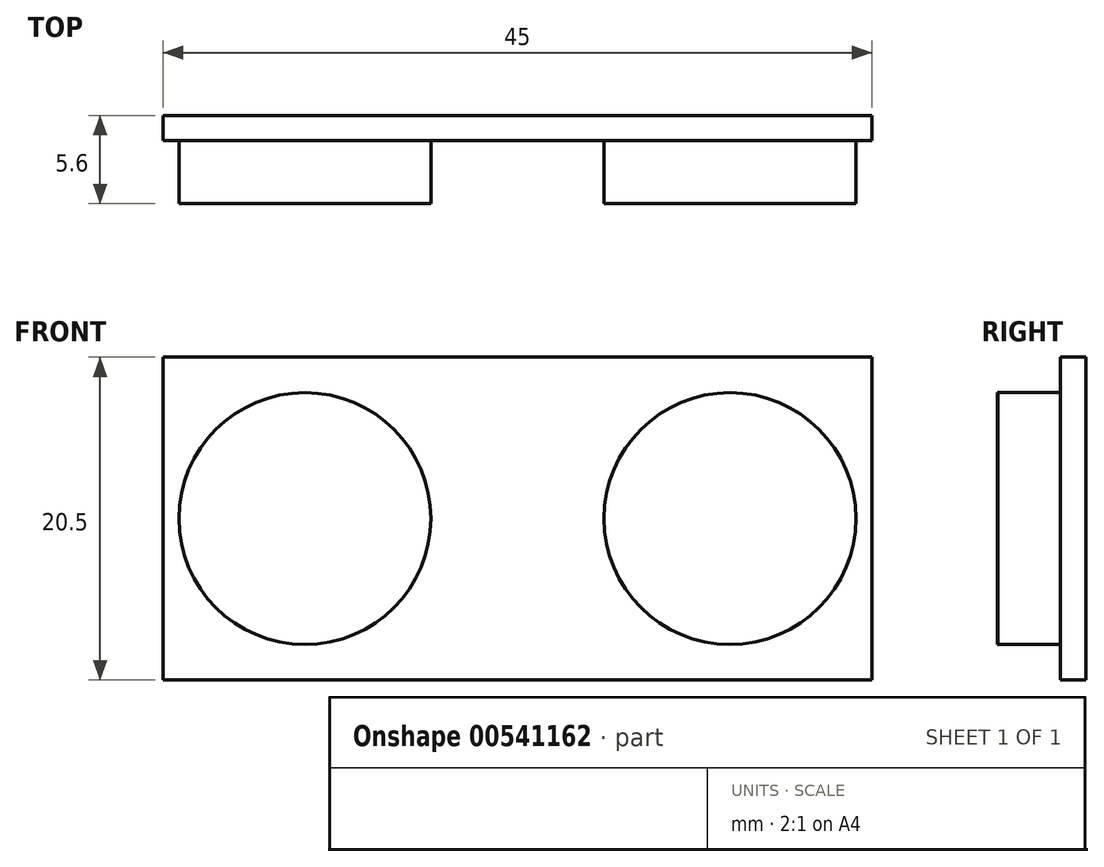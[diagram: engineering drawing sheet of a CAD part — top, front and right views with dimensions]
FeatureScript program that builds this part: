
annotation { "Feature Type Name" : "Feature", "Feature Type Description" : "" }
export const myFeature = defineFeature(function(context is Context, id is Id, definition is map)
    precondition{}
    {
        {
            var Q0;
            Q0=qCreatedBy(makeId("Front.planeOp"),FACE);
            var sketch = newSketch(context, id + "F0", { "sketchPlane" : qUnion([Q0])});
            skLineSegment(sketch, "E0.bottom", {"start": v(-22.5, 10.25) * mm, "end": v(22.5, 10.25) * mm});
            skLineSegment(sketch, "E0.top", {"start": v(-22.5, -10.25) * mm, "end": v(22.5, -10.25) * mm});
            skLineSegment(sketch, "E0.left", {"start": v(-22.5, 10.25) * mm, "end": v(-22.5, -10.25) * mm});
            skLineSegment(sketch, "E0.right", {"start": v(22.5, 10.25) * mm, "end": v(22.5, -10.25) * mm});
            skPoint(sketch, "E0.middle", {"position": v(0, 0) * mm});
            skSolve(sketch);
        }
        {
            var Q0;
            Q0 = qSketchRegion(id + "F0", true);
            extrude(context, id + "F1", {"entities" : qUnion([Q0]), "depth" : 1.6 * mm, "offsetDistance" : 25.4 * mm});
        }
        {
            var Q0;
            Q0=makeQuery(id+"F1.opExtrude","CAP_FACE",FACE,{"disambiguationData":[OSD([sQuery(id+"F0.wireOp",EDGE,"E0.bottom"),sQuery(id+"F0.wireOp",EDGE,"E0.top"),sQuery(id+"F0.wireOp",EDGE,"E0.left"),sQuery(id+"F0.wireOp",EDGE,"E0.right")])],"isStart":false});
            var sketch = newSketch(context, id + "F2", { "sketchPlane" : qUnion([Q0])});
            skCircle(sketch, "E1", {"center": v(-13.5, 0) * mm, "radius": 8 * mm});
            skCircle(sketch, "E2", {"center": v(13.5, 0) * mm, "radius": 8 * mm});
            skPoint(sketch, "E3", {"position": v(0, 0) * mm});
            skLineSegment(sketch, "E4", {"start": v(0, 10.25) * mm, "end": v(0, -10.25) * mm});
            skLineSegment(sketch, "E5", {"start": v(-5.5, 0) * mm, "end": v(5.5, 0) * mm});
            skSolve(sketch);
        }
        {
            var Q0;
            Q0=makeQuery(id+"F2.imprint","IMPRINT",FACE,{"disambiguationData":[TD([[makeQuery(id+"F2.imprint","IMPRINT",EDGE,{"derivedFrom":sQuery(id+"F2.wireOp",EDGE,"E1")}),1.0]])]});
            extrude(context, id + "F3", {"entities" : qUnion([Q0]), "operationType" : NewBodyOperationType.ADD, "depth" : 4 * mm, "offsetDistance" : 25.4 * mm});
        }
        {
            var Q0;
            Q0=makeQuery(id+"F2.imprint","IMPRINT",FACE,{"disambiguationData":[TD([[makeQuery(id+"F2.imprint","IMPRINT",EDGE,{"derivedFrom":sQuery(id+"F2.wireOp",EDGE,"E2")}),1.0]])]});
            extrude(context, id + "F4", {"entities" : qUnion([Q0]), "operationType" : NewBodyOperationType.ADD, "depth" : 4 * mm, "offsetDistance" : 25.4 * mm});
        }
    });
